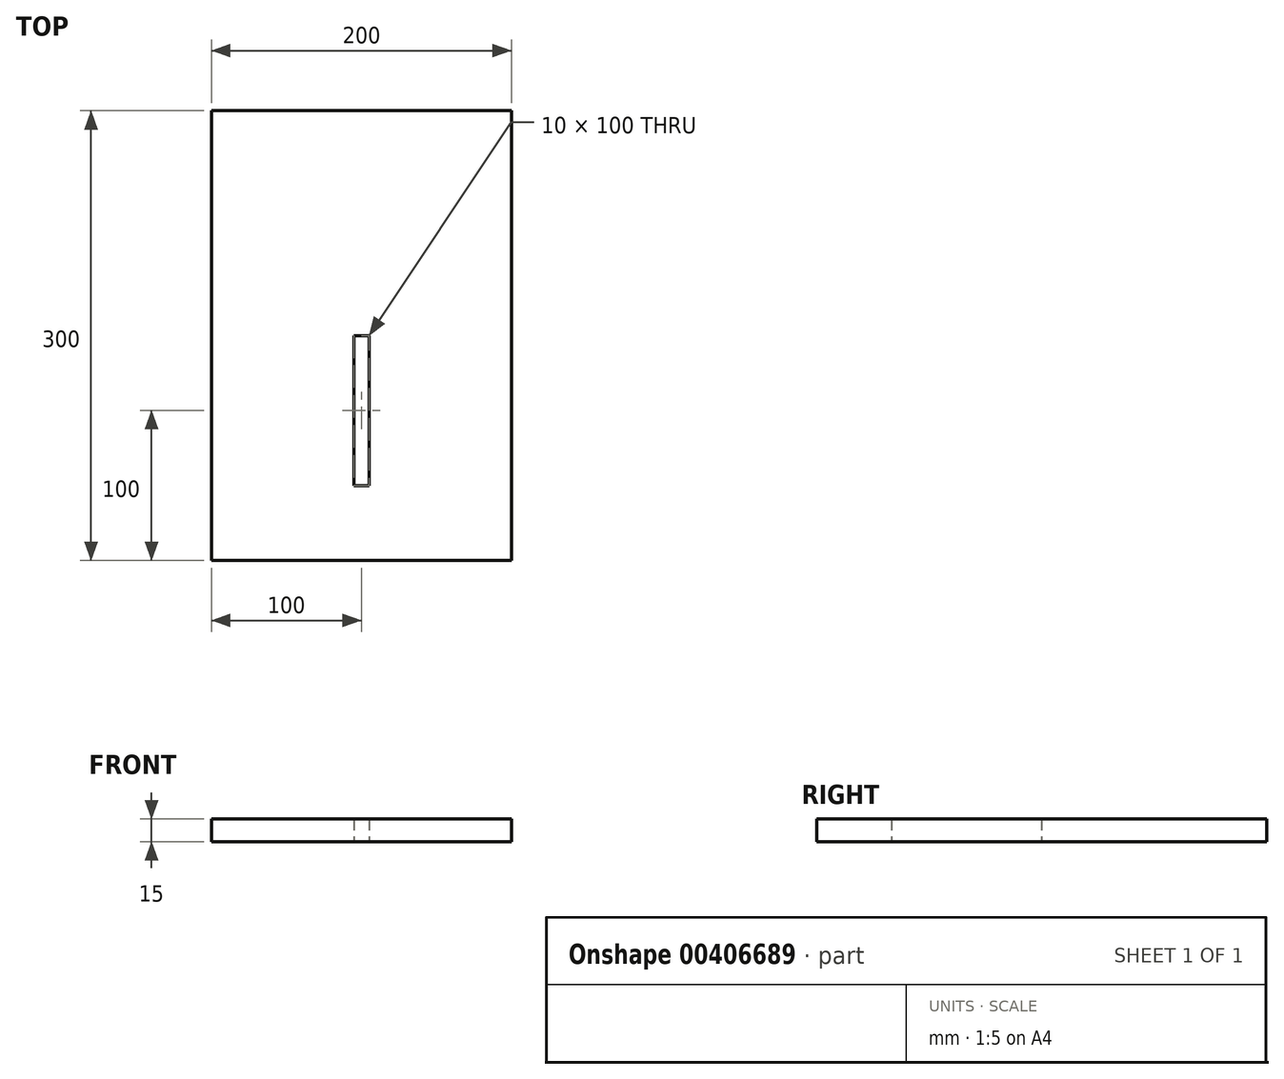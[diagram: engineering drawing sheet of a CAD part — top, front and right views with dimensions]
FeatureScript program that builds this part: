
annotation { "Feature Type Name" : "Feature", "Feature Type Description" : "" }
export const myFeature = defineFeature(function(context is Context, id is Id, definition is map)
    precondition{}
    {
        {
            var Q0;
            Q0=qCreatedBy(makeId("Top.planeOp"),FACE);
            var sketch = newSketch(context, id + "F0", { "sketchPlane" : qUnion([Q0])});
            skLineSegment(sketch, "E0", {"start": v(0, 0) * mm, "end": v(200, 0) * mm});
            skLineSegment(sketch, "E1", {"start": v(200, 0) * mm, "end": v(200, 300) * mm});
            skLineSegment(sketch, "E2", {"start": v(200, 300) * mm, "end": v(0, 300) * mm});
            skLineSegment(sketch, "E3", {"start": v(0, 300) * mm, "end": v(0, 0) * mm});
            skPoint(sketch, "E4.orphan", {"position": v(100, 300) * mm});
            skPoint(sketch, "E5.orphan", {"position": v(100, 0) * mm});
            skLineSegment(sketch, "E6.0", {"start": v(95, 150) * mm, "end": v(95, 50) * mm});
            skLineSegment(sketch, "E7.0", {"start": v(105, 150) * mm, "end": v(105, 50) * mm});
            skLineSegment(sketch, "E8", {"start": v(95, 50) * mm, "end": v(105, 50) * mm});
            skLineSegment(sketch, "E9", {"start": v(95, 150) * mm, "end": v(105, 150) * mm});
            skSolve(sketch);
        }
        {
            var Q0;
            Q0 = qSketchRegion(id + "F0", true);
            extrude(context, id + "F1", {"entities" : qUnion([Q0]), "depth" : 15 * mm});
        }
    });
